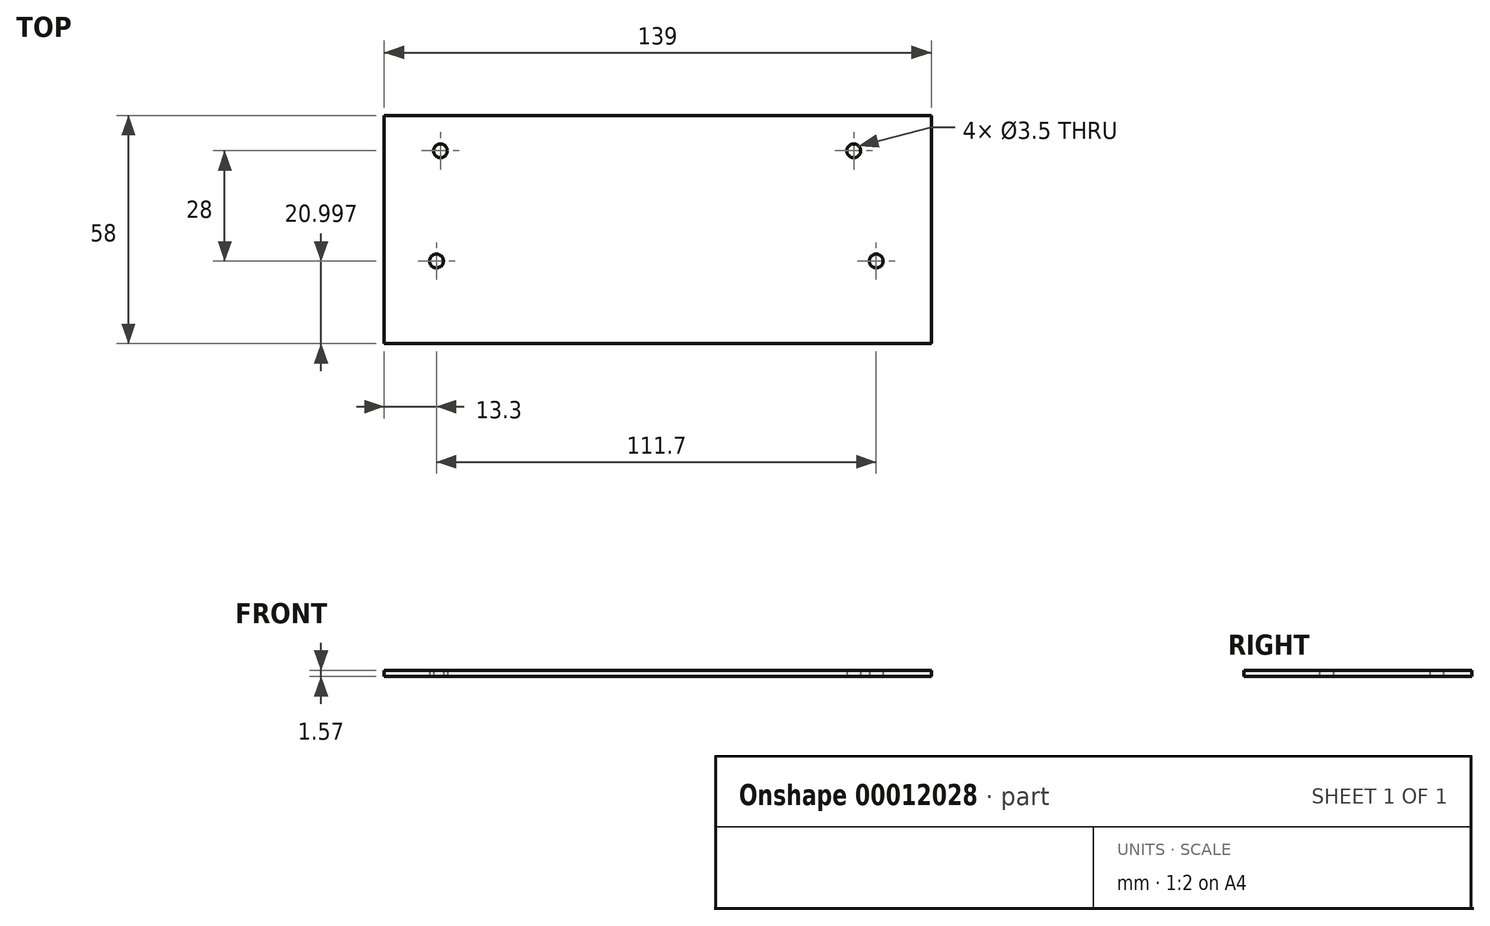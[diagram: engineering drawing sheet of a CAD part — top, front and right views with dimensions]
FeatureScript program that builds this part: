
annotation { "Feature Type Name" : "Feature", "Feature Type Description" : "" }
export const myFeature = defineFeature(function(context is Context, id is Id, definition is map)
    precondition{}
    {
        {
            var Q0;
            Q0=qCreatedBy(makeId("Top.planeOp"),FACE);
            var sketch = newSketch(context, id + "F0", { "sketchPlane" : qUnion([Q0])});
            skLineSegment(sketch, "E0.rect.bottom", {"start": v(69.5, 25.73) * mm, "end": v(-69.5, 25.73) * mm});
            skLineSegment(sketch, "E0.rect.top", {"start": v(69.5, -32.27) * mm, "end": v(-69.5, -32.27) * mm});
            skLineSegment(sketch, "E0.rect.left", {"start": v(69.5, 25.73) * mm, "end": v(69.5, -32.27) * mm});
            skLineSegment(sketch, "E0.rect.right", {"start": v(-69.5, 25.73) * mm, "end": v(-69.5, -32.27) * mm});
            skPoint(sketch, "E0.rect.middle", {"position": v(0, -3.27) * mm});
            skCircle(sketch, "E1", {"center": v(-55.2, 16.73) * mm, "radius": 1.75 * mm});
            skCircle(sketch, "E2", {"center": v(-56.2, -11.27) * mm, "radius": 1.75 * mm});
            skCircle(sketch, "E3", {"center": v(49.8, 16.73) * mm, "radius": 1.75 * mm});
            skCircle(sketch, "E4", {"center": v(55.5, -11.27) * mm, "radius": 1.75 * mm});
            skSolve(sketch);
        }
        {
            var Q0;
            Q0 = qSketchRegion(id + "F0", true);
            extrude(context, id + "F1", {"entities" : qUnion([Q0]), "depth" : 1.57 * mm});
        }
    });
